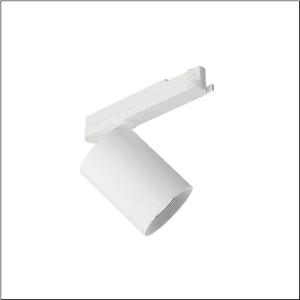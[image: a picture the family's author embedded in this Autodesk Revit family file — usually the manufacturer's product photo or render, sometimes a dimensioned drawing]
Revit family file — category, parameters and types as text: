
# Revit family: spot_21_51se13dba5b
name_source: partatom
category: Lighting Fixtures
units: mm (PartAtom-declared; Revit-internal decimal feet)

## family parameters
Cut with Voids When Loaded = No
Host = Face
Light Source = No
Part Type = Normal
Room Calculation Point = No
Round Connector Dimension = Use Diameter
Shared = No

## types (1)
- --- (1 x LED, 5190 lm, 42.4 W, 2700K)
    Apparent Load = 42 VA
    CIE Flux Codes = 95 98 99 100 100
    Color Rendering = 90
    Color Temperature = 2700K
    Default Elevation = 1800 mm
    Description = Spot 21, directional spotlight, light control with lens, of PMMA, LED rated luminous flux: 4.960lm, light colour: 927, control gear: ECG Multilumen, with 3-phase adapter, mains connection: 220..240V, AC, 50/60Hz, of aluminium, traffic white (RAL 9016), length: 253mm, diameter: 105mm, protection rating (complete): IP20, insulation class (complete): insulation class I (protective earthing), certification: CE, impact resistance: IK02, permissible ambient temperature for indoor applications: -20..+40°C, packaging unit: 1 piece
    Height = 175 mm
    Lamp = 1 x LED
    Lamp Light Flux = 5190 lm
    Lamp Power = 42.4 W
    Lamp count = 1
    Length = 105 mm
    Luminous efficacy = 122 lm/W
    Manufacturer = Siteco
    ModVariant = No
    Model = 51SE13DBA5B
    Mounting Place = Ceiling
    Mounting Type = Pendant
    Number of Poles = 1
    OnlyDefault = Yes
    Power Factor = 1
    Product Name = Spot 21
    Product group = directional spotlight
    ProductGroupID = 905
    Protection Class = Protection class I
    Protection Degree = IP 20
    RLX_Detail_Level = 1
    RLX_Emergency_Light_Flux = 0 lm
    RLX_Emergency_Type = 0
    RLX_Emergency_Type_DB = No
    RlxData = <blob elided: 17581 chars, md5=efeead3e>
    Socket = socket
    Standby Power = 0 W
    System Light Flux = 5190 lm
    System Power = 42 W
    Type Comments = factory setting: luminous flux: 100 % | (ON | ON | ON | ON) | 1050 mA
    Type Image = l_1003976.jpg
    URL = http://relux.com
    VarID = @adj_075285
    Voltage = 0 V
    Weight = 0.00 kg
    Width = 0 mm  [stored 0 ft]

note: [stored X ft] marks values corroborated as IEEE doubles in the binary element streams (Revit-internal decimal feet)

## geometry (parser evidence)
native form markers: Blend x4, Sweep x10
no freeform markers — native parametric forms only
